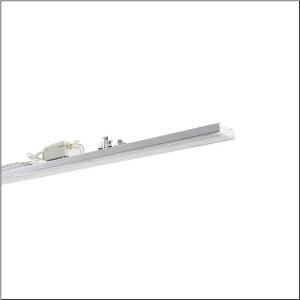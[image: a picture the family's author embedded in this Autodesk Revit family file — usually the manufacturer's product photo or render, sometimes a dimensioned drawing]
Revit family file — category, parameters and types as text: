
# Revit family: licross_11_recessed_mo_51tl1emn495g
name_source: partatom
category: Lighting Fixtures
units: mm (PartAtom-declared; Revit-internal decimal feet)

## family parameters
Cut with Voids When Loaded = No
Host = Face
Light Source = No
Part Type = Normal
Room Calculation Point = No
Round Connector Dimension = Use Diameter
Shared = No

## types (1)
- --- (1 x LED, 9950 lm, 55.2 W, 4000K)
    Apparent Load = 55 VA
    CIE Flux Codes = 85 95 99 100 100
    Color Rendering = 80
    Color Temperature = 4000K
    Default Elevation = 1800 mm
    Description = Licross 11 Recessed MO, luminaire insert, of sheet steel, coil coated, white, length: 1.500mm, width: 66mm, height: 67mm, LED rated luminous flux: 9.950lm, light colour: 840, SDCM (Standard Deviation of Colour Matching)MacAdam ≤ 2 SDCM (initial), control gear: ON/OFF Multilumen, with plug, 3-pole, with phase selection, mains connection: 220..240V, AC, 50/60Hz, rated input power: 55W, internal wiring halogen-free, primary light control with lens, of plastic, primary optical cover: cover, of PMMA, light emission: direct distribution, primary light characteristic: symmetric, protection rating (complete): IP40, insulation class (complete): insulation class I (protective earthing), certification: CE, ENEC, VDE, UKCA, protection symbol: D if used in an environment without relevant dust loads with corresponding accessories, impact resistance: IK06, permissible ambient temperature for indoor applications: -35..+40°C, corresponds to IFS (International Featured Standards) requirements for safety and quality in the food industry, reducing of maximum allowable ambient temperature of 5°C with ceiling mounting, The light source and the operating device comply with the requirements of the Ecodesign Regulation (EU) 2019/2020 and are replaceable in accordance with this regulation, packaging unit: 1 piece
    Height = 58 mm
    Lamp = 1 x LED
    Lamp Light Flux = 9950 lm
    Lamp Power = 55.2 W
    Lamp count = 1
    Length = 1500 mm
    Luminous efficacy = 180 lm/W
    Manufacturer = Siteco
    ModVariant = No
    Model = 51TL1EMN495G
    Mounting Place = Ceiling
    Mounting Type = Pendant
    Number of Poles = 1
    OnlyDefault = Yes
    Power Factor = 1
    Product Name = Licross 11 Recessed MO
    Product group = luminaire insert | ceiling pendant
    ProductGroupID = 901
    Protection Class = Protection class I
    Protection Degree = IP 40
    RLX_Detail_Level = 1
    RLX_Emergency_Light_Flux = 0 lm
    RLX_Emergency_Type = 0
    RLX_Emergency_Type_DB = No
    RlxData = <blob elided: 22617 chars, md5=310571de>
    Socket = socket
    Standby Power = 0 W
    System Light Flux = 9950 lm
    System Power = 55 W
    Type Comments = factory setting: luminous flux: 100 % | (A | C | E) | 126 mA
    Type Image = l_1296930.jpg
    URL = http://relux.com
    VarID = @adj_090863
    Voltage = 0 V
    Weight = 0.00 kg
    Width = 66 mm

## geometry (parser evidence)
native form markers: Blend x4, Sweep x10
no freeform markers — native parametric forms only
